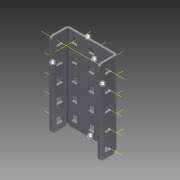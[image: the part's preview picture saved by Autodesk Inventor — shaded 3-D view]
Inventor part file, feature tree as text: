
AUTODESK INVENTOR PART (.ipt)
format: ipt  version: 2015 SP1 (Build 190203100, 203)  size: 1,891,328 bytes
history: native  units: in
note: dims shown in document units (in); Inventor stores cm internally (conversion verified against a paired STEP export)
features: other x31, pattern_linear x2, sheet_metal_op x1, extrude x1, imported_body x1, sketch x1
ambient origin geometry x8: Origin, YZ Plane, XZ Plane, XY Plane, X Axis, Y Axis, Z Axis, Center Point
bodies: Body1 (feature_tree)
feature tree (37):
  sheet_metal_op  "Fold1"
  other  "C-Channel"
  extrude  "length cut"  Depth=1.1811in
  other  "Work Point1"
  other  "Work Point2"
  other  "Work Point3"
  other  "top axis"
  other  "front axis"
  other  "back axis"
  pattern_linear  "top axes"  Count1=5  [1 undecoded]
  pattern_linear  "horiz axes"  Spacing1=0.5in  [1 undecoded]
  other  "Left Plane"
  other  "Right Plane"
  imported_body  "Base1"
  sketch  "Sketch1"  dims[d1=0.0in d2=1.1811in d4=0.5in d5=1.9685in d7=0.5in d8=1.9685in d10=0.5in d12=-2.5in d17=0.0in d18=0.0in d19=0.0in d20=0.0in d21=0.0in]
  other  "Work Axis4"
  other  "Work Axis5"
  other  "Work Axis6"
  other  "Work Axis7"
  other  "Work Axis8"
  other  "Work Axis9"
  other  "Work Axis10"
  other  "Work Axis11"
  other  "Work Axis12"
  other  "Work Axis13"
  other  "Work Axis14"
  other  "Work Axis15"
  other  "Work Axis16"
  other  "Work Axis17"
  other  "Work Axis48"
  other  "Work Axis49"
  other  "Work Axis50"
  other  "Work Axis51"
  other  "Work Axis62"
  other  "Work Axis63"
  other  "Work Axis64"
  other  "Work Axis65"
note: 2 required parameter values undecoded (feature->parameter linkage not recoverable at this tier; creation-order binding heuristic only, values carry confidence <= 0.55)
